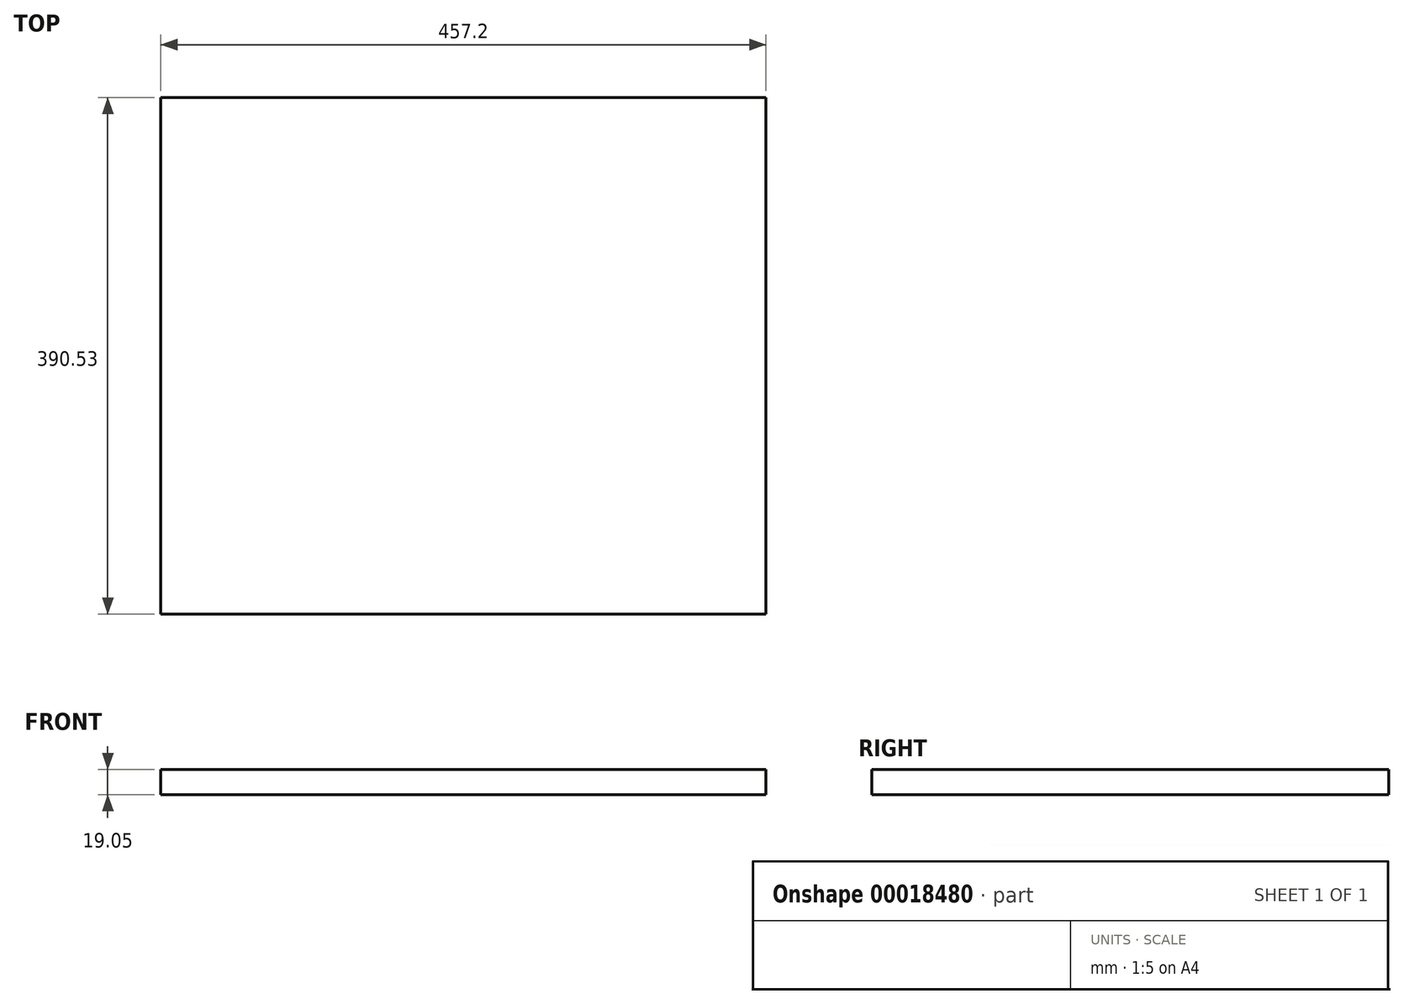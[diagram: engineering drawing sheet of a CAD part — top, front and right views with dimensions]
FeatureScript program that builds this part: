
annotation { "Feature Type Name" : "Feature", "Feature Type Description" : "" }
export const myFeature = defineFeature(function(context is Context, id is Id, definition is map)
    precondition{}
    {
        {
            var Q0;
            Q0=qCreatedBy(makeId("Top.planeOp"),FACE);
            var sketch = newSketch(context, id + "F0", { "sketchPlane" : qUnion([Q0])});
            skLineSegment(sketch, "E0.bottom", {"start": v(0, 0) * mm, "end": v(457.2, 0) * mm});
            skLineSegment(sketch, "E0.top", {"start": v(0, 390.53) * mm, "end": v(457.2, 390.53) * mm});
            skLineSegment(sketch, "E0.left", {"start": v(0, 0) * mm, "end": v(0, 390.53) * mm});
            skLineSegment(sketch, "E0.right", {"start": v(457.2, 0) * mm, "end": v(457.2, 390.53) * mm});
            skSolve(sketch);
        }
        {
            var Q0;
            Q0=makeQuery(id+"F0.imprint","IMPRINT",FACE,{"disambiguationData":[TD([[makeQuery(id+"F0.imprint","IMPRINT",EDGE,{"derivedFrom":sQuery(id+"F0.wireOp",EDGE,"E0.bottom")}),1.0]])]});
            extrude(context, id + "F1", {"entities" : qUnion([Q0]), "oppositeDirection" : true, "depth" : 19.05 * mm});
        }
    });
